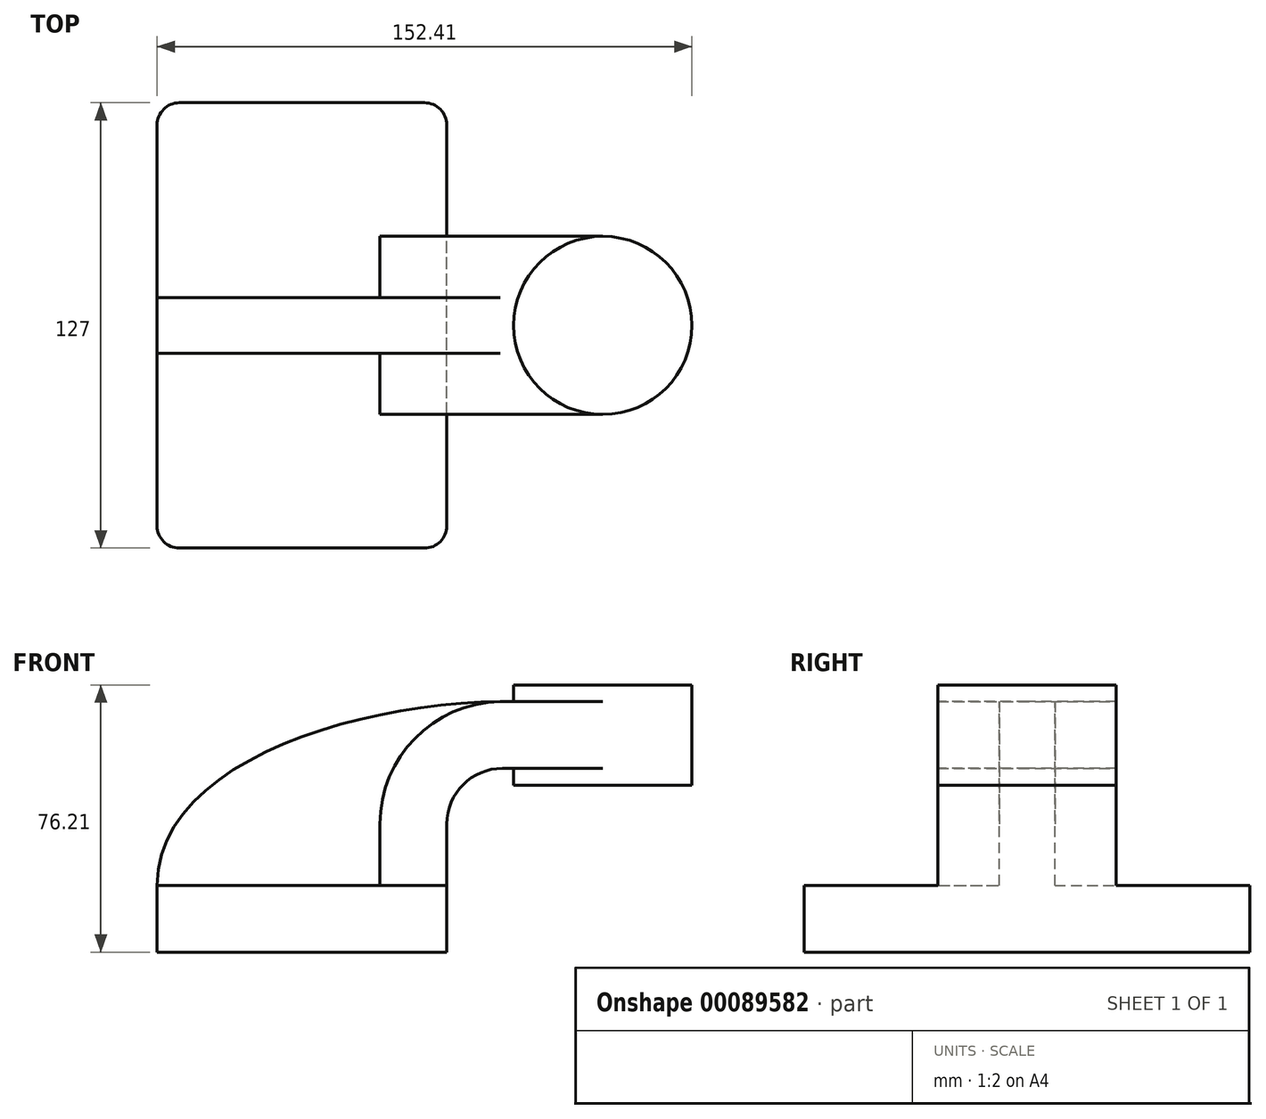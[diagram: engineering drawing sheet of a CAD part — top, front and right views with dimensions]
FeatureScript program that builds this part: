
annotation { "Feature Type Name" : "Feature", "Feature Type Description" : "" }
export const myFeature = defineFeature(function(context is Context, id is Id, definition is map)
    precondition{}
    {
        {
            var Q0;
            Q0=qCreatedBy(makeId("Front.planeOp"),FACE);
            var sketch = newSketch(context, id + "F0", { "sketchPlane" : qUnion([Q0])});
            skLineSegment(sketch, "E0.bottom", {"start": v(-41.28, 9.52) * mm, "end": v(41.28, 9.53) * mm});
            skLineSegment(sketch, "E0.top", {"start": v(-41.28, -9.53) * mm, "end": v(41.28, -9.53) * mm});
            skLineSegment(sketch, "E0.left", {"start": v(-41.28, 9.52) * mm, "end": v(-41.28, -9.53) * mm});
            skLineSegment(sketch, "E0.right", {"start": v(41.28, 9.53) * mm, "end": v(41.28, -9.52) * mm});
            skPoint(sketch, "E0.middle", {"position": v(0, 0) * mm});
            skLineSegment(sketch, "E1.bottom", {"start": v(60.32, 38.1) * mm, "end": v(111.12, 38.1) * mm});
            skLineSegment(sketch, "E1.top", {"start": v(60.32, 66.68) * mm, "end": v(111.12, 66.68) * mm});
            skLineSegment(sketch, "E1.left", {"start": v(60.33, 38.1) * mm, "end": v(60.32, 66.68) * mm});
            skLineSegment(sketch, "E1.right", {"start": v(111.12, 38.1) * mm, "end": v(111.12, 66.68) * mm});
            skPoint(sketch, "E1.middle", {"position": v(85.72, 52.39) * mm});
            skLineSegment(sketch, "E2", {"start": v(41.27, 9.53) * mm, "end": v(41.27, 27) * mm});
            skArc(sketch, "E3", {"start": v(41.27, 27) * mm, "mid": v(45.92, 38.23) * mm, "end": v(57.15, 42.88) * mm});
            skLineSegment(sketch, "E4", {"start": v(57.15, 42.88) * mm, "end": v(85.72, 42.88) * mm});
            skLineSegment(sketch, "E5.0", {"start": v(57.15, 61.93) * mm, "end": v(85.72, 61.93) * mm});
            skArc(sketch, "E5.1", {"start": v(22.22, 27) * mm, "mid": v(32.45, 51.7) * mm, "end": v(57.15, 61.93) * mm});
            skLineSegment(sketch, "E5.2", {"start": v(22.22, 9.53) * mm, "end": v(22.22, 27) * mm});
            skLineSegment(sketch, "E6", {"start": v(85.72, 38.1) * mm, "end": v(85.72, 66.68) * mm});
            skFitSpline(sketch, "E7", {"points": [v(-41.28, 9.52) * mm, v(57.15, 61.93) * mm], "startDerivative": vector(0.86, 105.97) * mm, "endDerivative": vector(124.35, 1) * mm});
            skSolve(sketch);
        }
        {
            var Q0;
            Q0=makeQuery(id+"F0.imprint","IMPRINT",FACE,{"disambiguationData":[TD([[makeQuery(id+"F0.imprint","IMPRINT",EDGE,{"derivedFrom":sQuery(id+"F0.wireOp",EDGE,"E0.top")}),1.0]])]});
            extrude(context, id + "F1", {"entities" : qUnion([Q0]), "depth" : 127 * mm, "symmetric" : true});
        }
        {
            var Q0;
            {var subQ1=sQuery(id+"F0.wireOp",EDGE,"E2");Q0=makeQuery(id+"F0.imprint","IMPRINT",FACE,{"disambiguationData":[TD([[makeQuery(id+"F0.imprint","IMPRINT",EDGE,{"derivedFrom":subQ1}),1.0]])]});}
            var Q1;
            {var subQ0=sQuery(id+"F0.wireOp",EDGE,"E4");var subQ1=sQuery(id+"F0.wireOp",EDGE,"E1.left");var subQ2=makeQuery(id+"F0.imprint","INTERSECT",VERTEX,{"derivedFrom":[subQ1,subQ0]});Q1=makeQuery(id+"F0.imprint","IMPRINT",FACE,{"disambiguationData":[TD([[makeQuery(id+"F0.imprint","IMPRINT",EDGE,{"disambiguationData":[TD([[subQ2,-1.0]])],"derivedFrom":subQ1}),-1.0]])]});}
            extrude(context, id + "F2", {"entities" : qUnion([Q0, Q1]), "operationType" : NewBodyOperationType.ADD, "depth" : 50.8 * mm, "symmetric" : true});
        }
        {
            var Q0;
            {var subQ3=sQuery(id+"F0.wireOp",EDGE,"E5.2");Q0=makeQuery(id+"F0.imprint","IMPRINT",FACE,{"disambiguationData":[TD([[makeQuery(id+"F0.imprint","IMPRINT",EDGE,{"derivedFrom":subQ3}),1.0]])]});}
            extrude(context, id + "F3", {"entities" : qUnion([Q0]), "operationType" : NewBodyOperationType.ADD, "depth" : 15.88 * mm, "symmetric" : true});
        }
        {
            var Q0;
            {var subQ0=sQuery(id+"F0.wireOp",EDGE,"E1.right");Q0=makeQuery(id+"F0.imprint","IMPRINT",FACE,{"disambiguationData":[TD([[makeQuery(id+"F0.imprint","IMPRINT",EDGE,{"derivedFrom":subQ0}),1.0]])]});}
            var Q1;
            Q1=sQuery(id+"F0.wireOp",EDGE,"E6");
            revolve(context, id + "F4", {"operationType" : NewBodyOperationType.ADD, "entities" : qUnion([Q0]), "axis" : qUnion([Q1]), "revolveType" : RevolveType.FULL});
        }
        {
            var Q0;
            Q0=makeQuery(id+"F1.opExtrude","CAP_EDGE",EDGE,{"disambiguationData":[OSD([sQuery(id+"F0.wireOp",EDGE,"E0.left")])],"isStart":false});
            var Q1;
            Q1=makeQuery(id+"F1.opExtrude","CAP_EDGE",EDGE,{"disambiguationData":[OSD([sQuery(id+"F0.wireOp",EDGE,"E0.right")])],"isStart":false});
            var Q2;
            Q2=makeQuery(id+"F1.opExtrude","CAP_EDGE",EDGE,{"disambiguationData":[OSD([sQuery(id+"F0.wireOp",EDGE,"E0.right")])],"isStart":true});
            var Q3;
            Q3=makeQuery(id+"F1.opExtrude","CAP_EDGE",EDGE,{"disambiguationData":[OSD([sQuery(id+"F0.wireOp",EDGE,"E0.left")])],"isStart":true});
            fillet(context, id + "F5", {"entities" : qUnion([Q0, Q1, Q2, Q3]), "radius" : 6.35 * mm, "tangentPropagation" : true, "allowEdgeOverflow" : false});
        }
    });
